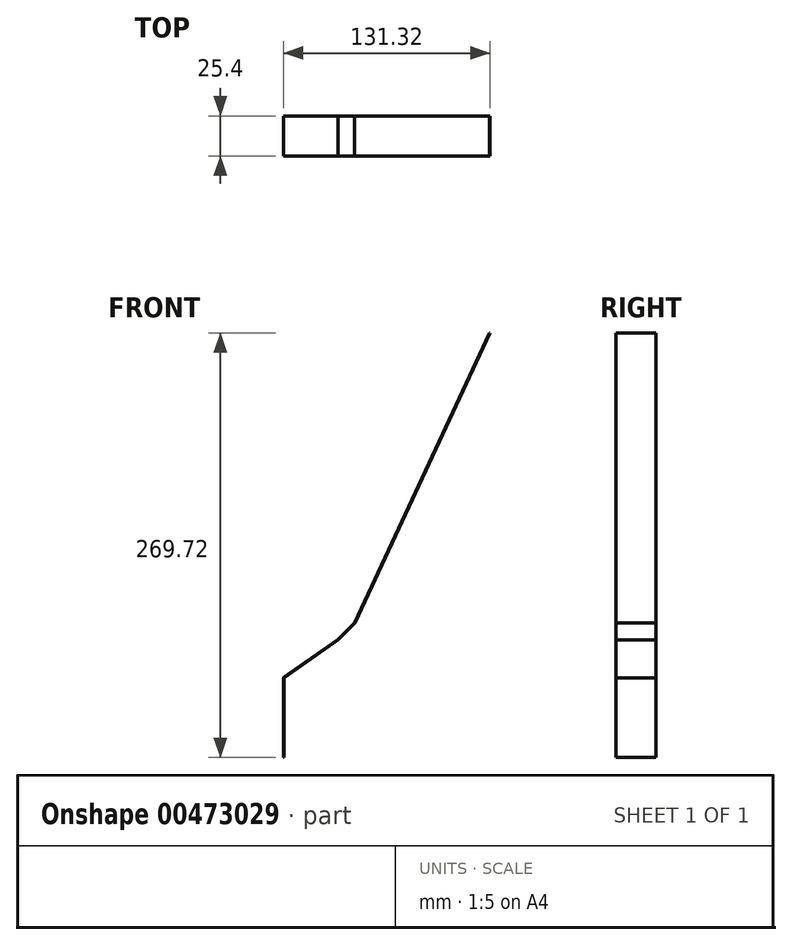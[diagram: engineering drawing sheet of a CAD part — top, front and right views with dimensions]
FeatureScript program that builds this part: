
annotation { "Feature Type Name" : "Feature", "Feature Type Description" : "" }
export const myFeature = defineFeature(function(context is Context, id is Id, definition is map)
    precondition{}
    {
        {
            var Q0;
            Q0=qCreatedBy(makeId("Front.planeOp"),FACE);
            var sketch = newSketch(context, id + "F0", { "sketchPlane" : qUnion([Q0])});
            skLineSegment(sketch, "E0", {"start": v(0, 0) * mm, "end": v(34.48, 24.15) * mm});
            skLineSegment(sketch, "E1", {"start": v(34.48, 24.15) * mm, "end": v(45.13, 34.79) * mm});
            skLineSegment(sketch, "E2", {"start": v(45.13, 34.79) * mm, "end": v(131, 218.95) * mm});
            skLineSegment(sketch, "E3.0", {"start": v(-0.32, 0.17) * mm, "end": v(34.3, 24.4) * mm});
            skLineSegment(sketch, "E4.0", {"start": v(34.26, 24.37) * mm, "end": v(44.9, 35.01) * mm});
            skLineSegment(sketch, "E5.0", {"start": v(44.84, 34.92) * mm, "end": v(130.72, 219.09) * mm});
            skLineSegment(sketch, "E6", {"start": v(130.72, 219.09) * mm, "end": v(131, 218.95) * mm});
            skLineSegment(sketch, "E7", {"start": v(-0.32, 0.17) * mm, "end": v(-0.32, -50.63) * mm});
            skLineSegment(sketch, "E8", {"start": v(-0.32, -50.63) * mm, "end": v(0, -50.63) * mm});
            skLineSegment(sketch, "E9", {"start": v(0, -50.63) * mm, "end": v(0, 0) * mm});
            skSolve(sketch);
        }
        {
            var Q0;
            Q0 = qSketchRegion(id + "F0", true);
            extrude(context, id + "F1", {"entities" : qUnion([Q0]), "oppositeDirection" : true, "depth" : 25.4 * mm});
        }
    });
